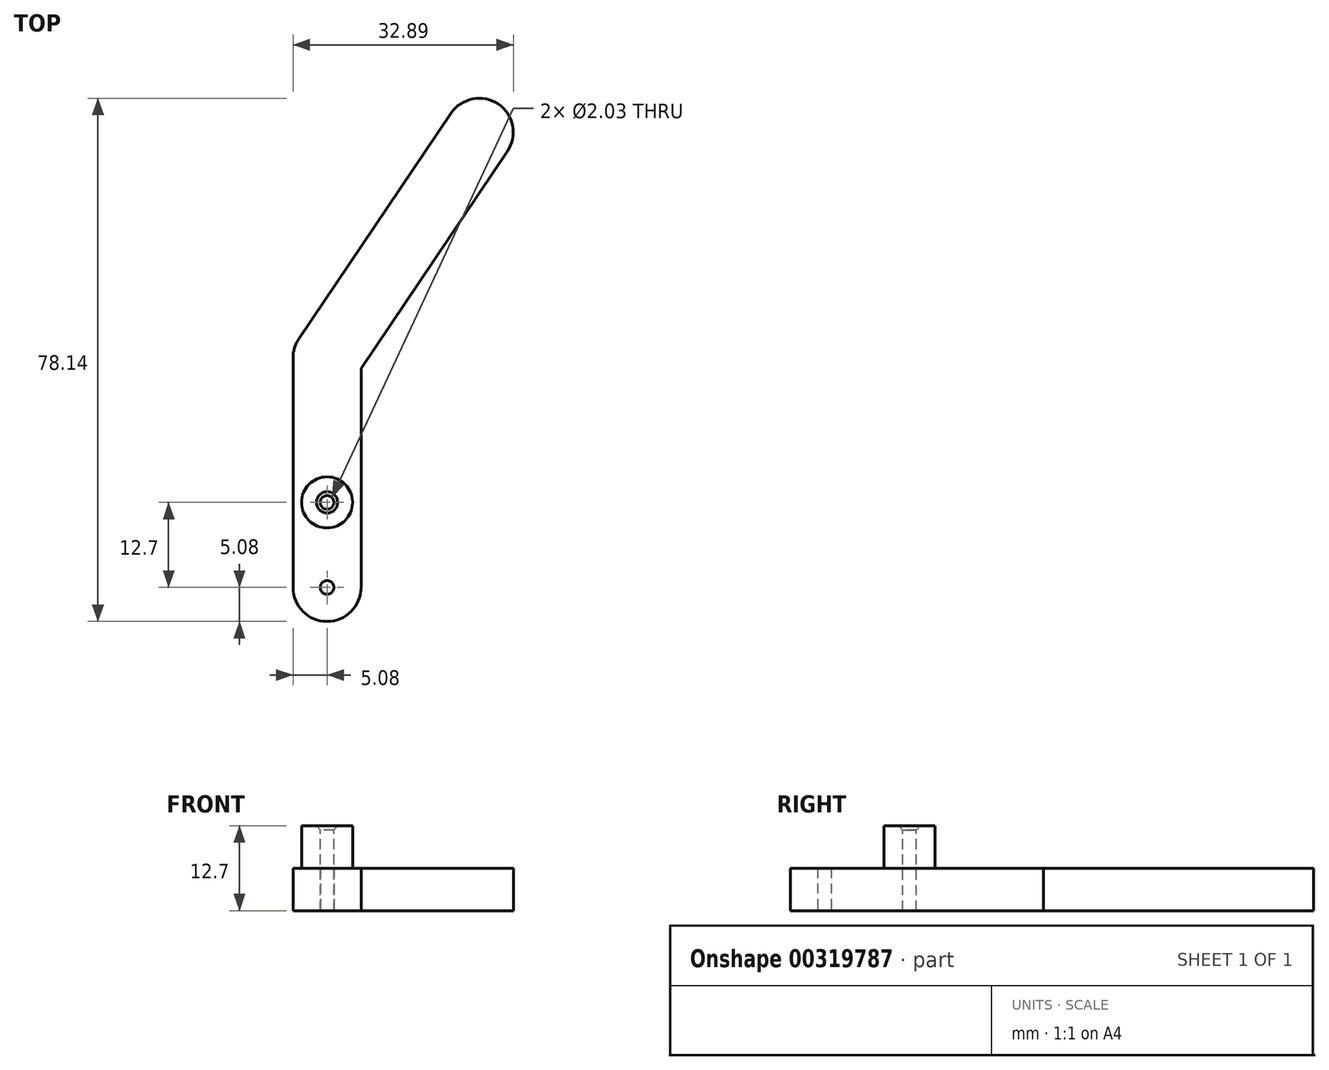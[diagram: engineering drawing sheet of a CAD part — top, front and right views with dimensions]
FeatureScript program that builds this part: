
annotation { "Feature Type Name" : "Feature", "Feature Type Description" : "" }
export const myFeature = defineFeature(function(context is Context, id is Id, definition is map)
    precondition{}
    {
        {
            var Q0;
            Q0=qCreatedBy(makeId("Top.planeOp"),FACE);
            var sketch = newSketch(context, id + "F0", { "sketchPlane" : qUnion([Q0])});
            skLineSegment(sketch, "E0", {"start": v(0, 0) * mm, "end": v(0, 12.7) * mm});
            skLineSegment(sketch, "E1", {"start": v(0, 12.7) * mm, "end": v(0, 34.3) * mm});
            skLineSegment(sketch, "E2", {"start": v(0, 34.3) * mm, "end": v(22.73, 67.98) * mm});
            skArc(sketch, "E3.0.startCap", {"start": v(4.21, 31.45) * mm, "mid": v(-2.84, 30.08) * mm, "end": v(-4.21, 37.13) * mm});
            skArc(sketch, "E3.0.endCap", {"start": v(18.51, 70.82) * mm, "mid": v(25.57, 72.2) * mm, "end": v(26.94, 65.14) * mm});
            skLineSegment(sketch, "E3.0.left", {"start": v(-4.21, 37.13) * mm, "end": v(18.51, 70.82) * mm});
            skLineSegment(sketch, "E3.0.right", {"start": v(4.21, 31.45) * mm, "end": v(26.94, 65.14) * mm});
            skArc(sketch, "E3.1.startCap", {"start": v(5.08, 12.7) * mm, "mid": v(0, 7.62) * mm, "end": v(-5.08, 12.7) * mm});
            skArc(sketch, "E3.1.endCap", {"start": v(-5.08, 34.3) * mm, "mid": v(0, 39.37) * mm, "end": v(5.08, 34.3) * mm});
            skLineSegment(sketch, "E3.1.left", {"start": v(-5.08, 12.7) * mm, "end": v(-5.08, 34.3) * mm});
            skLineSegment(sketch, "E3.1.right", {"start": v(5.08, 12.7) * mm, "end": v(5.08, 34.3) * mm});
            skArc(sketch, "E3.2.startCap", {"start": v(5.08, 0) * mm, "mid": v(0, -5.08) * mm, "end": v(-5.08, 0) * mm});
            skArc(sketch, "E3.2.endCap", {"start": v(-5.08, 12.7) * mm, "mid": v(0, 17.78) * mm, "end": v(5.08, 12.7) * mm});
            skLineSegment(sketch, "E3.2.left", {"start": v(-5.08, 0) * mm, "end": v(-5.08, 12.7) * mm});
            skLineSegment(sketch, "E3.2.right", {"start": v(5.08, 0) * mm, "end": v(5.08, 12.7) * mm});
            skSolve(sketch);
        }
        {
            var Q0;
            Q0 = qSketchRegion(id + "F0", true);
            extrude(context, id + "F1", {"entities" : qUnion([Q0]), "depth" : 6.35 * mm});
        }
        {
            var Q0;
            Q0=makeQuery(id+"F1.opExtrude","CAP_FACE",FACE,{"disambiguationData":[OSD([sQuery(id+"F0.wireOp",EDGE,"E3.0.endCap"),sQuery(id+"F0.wireOp",EDGE,"E3.0.left"),sQuery(id+"F0.wireOp",EDGE,"E3.0.right"),sQuery(id+"F0.wireOp",EDGE,"E3.1.endCap"),sQuery(id+"F0.wireOp",EDGE,"E3.1.left"),sQuery(id+"F0.wireOp",EDGE,"E3.1.right"),sQuery(id+"F0.wireOp",EDGE,"E3.2.startCap"),sQuery(id+"F0.wireOp",EDGE,"E3.2.left"),sQuery(id+"F0.wireOp",EDGE,"E3.2.right")])],"isStart":false});
            var sketch = newSketch(context, id + "F2", { "sketchPlane" : qUnion([Q0])});
            skCircle(sketch, "E4", {"center": v(0, 12.7) * mm, "radius": 3.81 * mm});
            skSolve(sketch);
        }
        {
            var Q0;
            Q0 = qSketchRegion(id + "F2", true);
            extrude(context, id + "F3", {"entities" : qUnion([Q0]), "operationType" : NewBodyOperationType.ADD, "depth" : 6.35 * mm});
        }
        {
            var Q0;
            Q0=makeQuery(id+"F3.opExtrude","CAP_FACE",FACE,{"disambiguationData":[OSD([sQuery(id+"F2.wireOp",EDGE,"E4")])],"isStart":false});
            var sketch = newSketch(context, id + "F4", { "sketchPlane" : qUnion([Q0])});
            skPoint(sketch, "E5", {"position": v(0, 12.7) * mm});
            skSolve(sketch);
        }
        {
            var Q0;
            Q0=sQuery(id+"F4.wireOp",VERTEX,"E5");
            var Q1;
            Q1=makeQuery(id+"F1.opExtrude","SWEPT_BODY",BODY,{"disambiguationData":[OSD([sQuery(id+"F0.wireOp",EDGE,"E3.0.endCap"),sQuery(id+"F0.wireOp",EDGE,"E3.0.left"),sQuery(id+"F0.wireOp",EDGE,"E3.0.right"),sQuery(id+"F0.wireOp",EDGE,"E3.1.endCap"),sQuery(id+"F0.wireOp",EDGE,"E3.1.left"),sQuery(id+"F0.wireOp",EDGE,"E3.1.right"),sQuery(id+"F0.wireOp",EDGE,"E3.2.startCap"),sQuery(id+"F0.wireOp",EDGE,"E3.2.left"),sQuery(id+"F0.wireOp",EDGE,"E3.2.right")])]});
            hole(context, id + "F5", {"style" : HoleStyle.C_SINK, "endStyle" : HoleEndStyle.THROUGH, "holeDiameter" : 2.03 * mm, "cSinkDiameter" : 3.17 * mm, "cSinkAngle" : 82 * degree, "tappedDepth" : 12.7 * mm, "tapClearance" : 3, "locations" : qUnion([Q0]), "scope" : qUnion([Q1])});
        }
        {
            var Q0;
            Q0=makeQuery(id+"F1.opExtrude","CAP_FACE",FACE,{"disambiguationData":[OSD([sQuery(id+"F0.wireOp",EDGE,"E3.0.endCap"),sQuery(id+"F0.wireOp",EDGE,"E3.0.left"),sQuery(id+"F0.wireOp",EDGE,"E3.0.right"),sQuery(id+"F0.wireOp",EDGE,"E3.1.endCap"),sQuery(id+"F0.wireOp",EDGE,"E3.1.left"),sQuery(id+"F0.wireOp",EDGE,"E3.1.right"),sQuery(id+"F0.wireOp",EDGE,"E3.2.startCap"),sQuery(id+"F0.wireOp",EDGE,"E3.2.left"),sQuery(id+"F0.wireOp",EDGE,"E3.2.right")])],"isStart":true});
            var sketch = newSketch(context, id + "F6", { "sketchPlane" : qUnion([Q0])});
            skPoint(sketch, "E6", {"position": v(0, 0) * mm});
            skSolve(sketch);
        }
        {
            var Q0;
            Q0=sQuery(id+"F6.wireOp",VERTEX,"E6");
            var Q1;
            Q1=makeQuery(id+"F1.opExtrude","SWEPT_BODY",BODY,{"disambiguationData":[OSD([sQuery(id+"F0.wireOp",EDGE,"E3.0.endCap"),sQuery(id+"F0.wireOp",EDGE,"E3.0.left"),sQuery(id+"F0.wireOp",EDGE,"E3.0.right"),sQuery(id+"F0.wireOp",EDGE,"E3.1.endCap"),sQuery(id+"F0.wireOp",EDGE,"E3.1.left"),sQuery(id+"F0.wireOp",EDGE,"E3.1.right"),sQuery(id+"F0.wireOp",EDGE,"E3.2.startCap"),sQuery(id+"F0.wireOp",EDGE,"E3.2.left"),sQuery(id+"F0.wireOp",EDGE,"E3.2.right")])]});
            hole(context, id + "F7", {"style" : HoleStyle.SIMPLE, "endStyle" : HoleEndStyle.THROUGH, "holeDiameter" : 2.03 * mm, "tappedDepth" : 12.7 * mm, "tapClearance" : 3, "locations" : qUnion([Q0]), "scope" : qUnion([Q1])});
        }
    });
